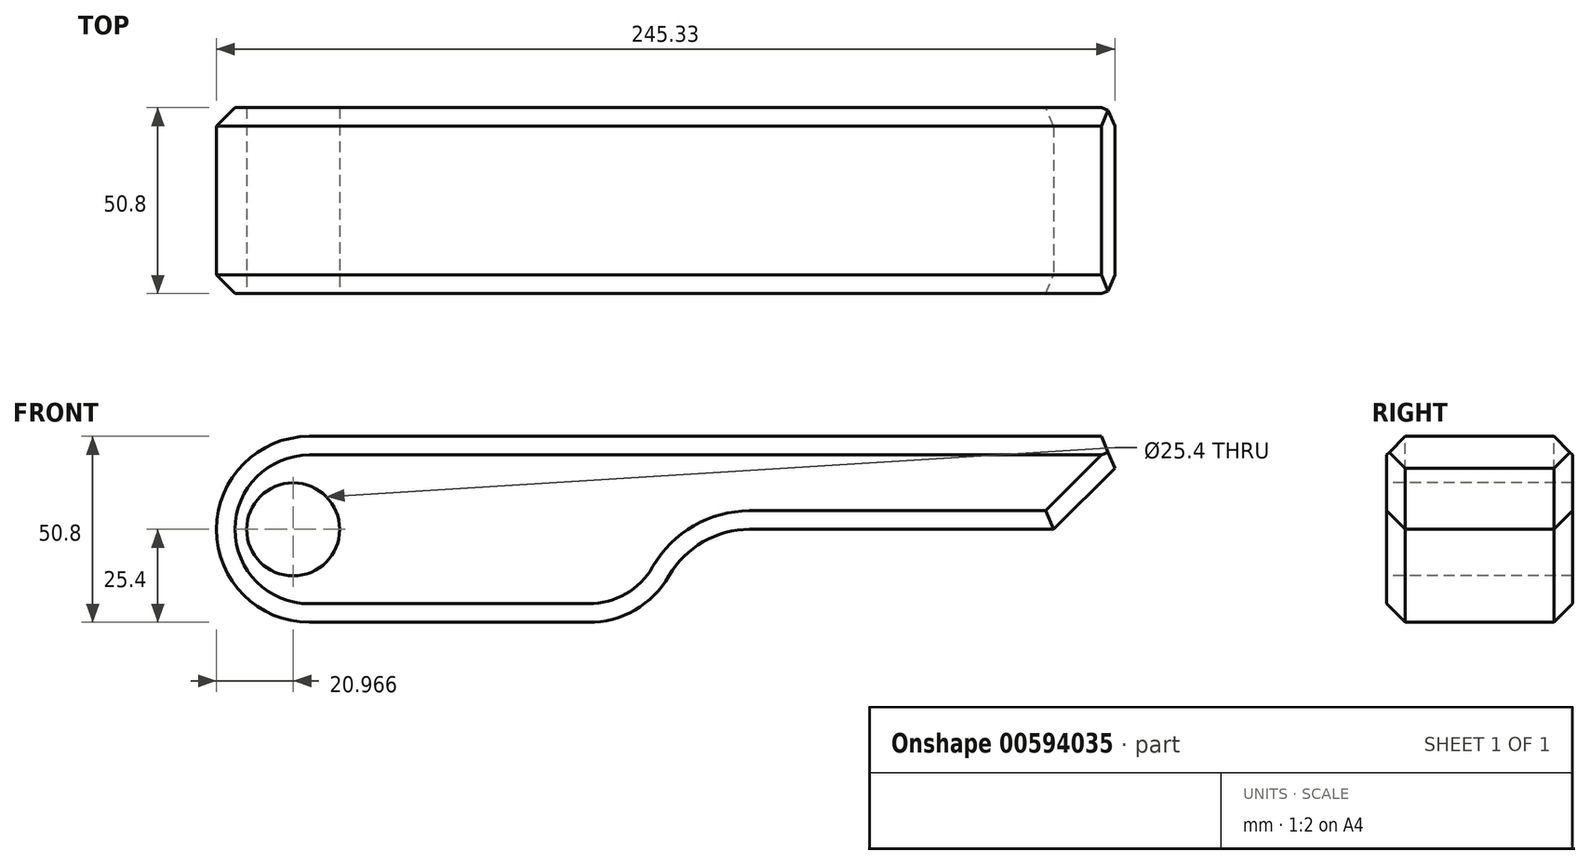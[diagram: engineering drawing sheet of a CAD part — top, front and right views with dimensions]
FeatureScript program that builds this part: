
annotation { "Feature Type Name" : "Feature", "Feature Type Description" : "" }
export const myFeature = defineFeature(function(context is Context, id is Id, definition is map)
    precondition{}
    {
        {
            var Q0;
            Q0=qCreatedBy(makeId("Top.planeOp"),FACE);
            var sketch = newSketch(context, id + "F0", { "sketchPlane" : qUnion([Q0])});
            skLineSegment(sketch, "E0.bottom", {"start": v(-73.3, 15.9) * mm, "end": v(180.7, 15.9) * mm});
            skLineSegment(sketch, "E0.top", {"start": v(-73.3, -34.9) * mm, "end": v(180.7, -34.9) * mm});
            skLineSegment(sketch, "E0.left", {"start": v(-73.3, 15.9) * mm, "end": v(-73.3, -34.9) * mm});
            skLineSegment(sketch, "E0.right", {"start": v(180.7, 15.9) * mm, "end": v(180.7, -34.9) * mm});
            skSolve(sketch);
        }
        {
            var Q0;
            Q0=makeQuery(id+"F0.imprint","IMPRINT",FACE,{"disambiguationData":[TD([[makeQuery(id+"F0.imprint","IMPRINT",EDGE,{"derivedFrom":sQuery(id+"F0.wireOp",EDGE,"E0.bottom")}),-1.0]])]});
            extrude(context, id + "F1", {"entities" : qUnion([Q0]), "depth" : 25.4 * mm, "offsetDistance" : 25.4 * mm});
        }
        {
            var Q0;
            Q0=makeQuery(id+"F1.opExtrude","CAP_FACE",FACE,{"disambiguationData":[OSD([sQuery(id+"F0.wireOp",EDGE,"E0.bottom"),sQuery(id+"F0.wireOp",EDGE,"E0.top"),sQuery(id+"F0.wireOp",EDGE,"E0.left"),sQuery(id+"F0.wireOp",EDGE,"E0.right")])],"isStart":true});
            var sketch = newSketch(context, id + "F2", { "sketchPlane" : qUnion([Q0])});
            skLineSegment(sketch, "E1.bottom", {"start": v(-73.3, 34.9) * mm, "end": v(53.7, 34.9) * mm});
            skLineSegment(sketch, "E1.top", {"start": v(-73.3, -15.9) * mm, "end": v(53.7, -15.9) * mm});
            skLineSegment(sketch, "E1.left", {"start": v(-73.3, 34.9) * mm, "end": v(-73.3, -15.9) * mm});
            skLineSegment(sketch, "E1.right", {"start": v(53.7, 34.9) * mm, "end": v(53.7, -15.9) * mm});
            skSolve(sketch);
        }
        {
            var Q0;
            Q0=makeQuery(id+"F2.imprint","IMPRINT",FACE,{"disambiguationData":[TD([[makeQuery(id+"F2.imprint","IMPRINT",EDGE,{"derivedFrom":sQuery(id+"F2.wireOp",EDGE,"E1.bottom")}),-1.0]])]});
            extrude(context, id + "F3", {"entities" : qUnion([Q0]), "operationType" : NewBodyOperationType.ADD, "depth" : 25.4 * mm, "offsetDistance" : 25.4 * mm});
        }
        {
            var Q0;
            Q0=makeQuery(id+"F3.boolean.opBoolean","MERGE",FACE,{"derivedFrom":[makeQuery(id+"F1.opExtrude","SWEPT_FACE",FACE,{"disambiguationData":[OSD([sQuery(id+"F0.wireOp",EDGE,"E0.top")])]}),makeQuery(id+"F3.opExtrude","SWEPT_FACE",FACE,{"disambiguationData":[OSD([sQuery(id+"F2.wireOp",EDGE,"E1.bottom")])]})]});
            var sketch = newSketch(context, id + "F4", { "sketchPlane" : qUnion([Q0])});
            skLineSegment(sketch, "E2", {"start": v(-73.3, 0) * mm, "end": v(53.7, 0) * mm});
            skSolve(sketch);
        }
        {
            var Q0;
            Q0=makeQuery(id+"F3.opExtrude","CAP_EDGE",EDGE,{"disambiguationData":[OSD([sQuery(id+"F2.wireOp",EDGE,"E1.left")])],"isStart":false});
            var Q1;
            Q1=makeQuery(id+"F1.opExtrude","CAP_EDGE",EDGE,{"disambiguationData":[OSD([sQuery(id+"F0.wireOp",EDGE,"E0.left")])],"isStart":false});
            fillet(context, id + "F5", {"entities" : qUnion([Q0, Q1]), "radius" : 25.4 * mm, "tangentPropagation" : true, "allowEdgeOverflow" : false});
        }
        {
            var Q0;
            Q0=makeQuery(id+"F3.opExtrude","CAP_EDGE",EDGE,{"disambiguationData":[OSD([sQuery(id+"F2.wireOp",EDGE,"E1.right")])],"isStart":false});
            fillet(context, id + "F6", {"entities" : qUnion([Q0]), "radius" : 25.4 * mm, "tangentPropagation" : true, "allowEdgeOverflow" : false});
        }
        {
            var Q0;
            {var subQ0=sQuery(id+"F4.wireOp",EDGE,"E2");Q0=makeQuery(id+"F4.imprint","IMPRINT",FACE,{"disambiguationData":[TD([[makeQuery(id+"F4.imprint","IMPRINT",EDGE,{"derivedFrom":subQ0}),-1.0]])]});}
            var sketch = newSketch(context, id + "F7", { "sketchPlane" : qUnion([Q0])});
            skCircle(sketch, "E3", {"center": v(-52.33, 0) * mm, "radius": 12.7 * mm});
            skSolve(sketch);
        }
        {
            var Q0;
            Q0=sQuery(id+"F7.wireOp",VERTEX,"E3.center");
            var Q1;
            Q1=makeQuery(id+"F1.opExtrude","SWEPT_BODY",BODY,{"disambiguationData":[OSD([sQuery(id+"F0.wireOp",EDGE,"E0.bottom"),sQuery(id+"F0.wireOp",EDGE,"E0.top"),sQuery(id+"F0.wireOp",EDGE,"E0.left"),sQuery(id+"F0.wireOp",EDGE,"E0.right")])]});
            hole(context, id + "F8", {"style" : HoleStyle.SIMPLE, "endStyle" : HoleEndStyle.BLIND, "holeDiameter" : 25.4 * mm, "majorDiameter" : 6.35 * mm, "holeDepth" : 50.8 * mm, "isTappedThrough" : true, "tappedDepth" : 12.7 * mm, "tapClearance" : 3, "locations" : qUnion([Q0]), "scope" : qUnion([Q1])});
        }
        {
            var Q0;
            Q0=makeQuery(id+"F6.opFillet","BLEND_EDGE",EDGE,{"blendedFrom":[makeQuery(id+"F3.opExtrude","CAP_EDGE",EDGE,{"disambiguationData":[OSD([sQuery(id+"F2.wireOp",EDGE,"E1.right")])],"isStart":false}),makeQuery(id+"F1.opExtrude","CAP_FACE",FACE,{"disambiguationData":[OSD([sQuery(id+"F0.wireOp",EDGE,"E0.bottom"),sQuery(id+"F0.wireOp",EDGE,"E0.top"),sQuery(id+"F0.wireOp",EDGE,"E0.left"),sQuery(id+"F0.wireOp",EDGE,"E0.right")])],"isStart":true})],"blendedInto":[makeQuery(id+"F1.opExtrude","CAP_FACE",FACE,{"disambiguationData":[OSD([sQuery(id+"F0.wireOp",EDGE,"E0.bottom"),sQuery(id+"F0.wireOp",EDGE,"E0.top"),sQuery(id+"F0.wireOp",EDGE,"E0.left"),sQuery(id+"F0.wireOp",EDGE,"E0.right")])],"isStart":true})]});
            fillet(context, id + "F9", {"entities" : qUnion([Q0]), "radius" : 25.4 * mm, "tangentPropagation" : true, "allowEdgeOverflow" : false});
        }
        {
            var Q0;
            Q0=makeQuery(id+"F1.opExtrude","CAP_EDGE",EDGE,{"disambiguationData":[OSD([sQuery(id+"F0.wireOp",EDGE,"E0.right")])],"isStart":true});
            chamfer(context, id + "F10", {"entities" : qUnion([Q0]), "width" : 25.4 * mm, "tangentPropagation" : true});
        }
        {
            var Q0;
            {var subQ0=sQuery(id+"F0.wireOp",EDGE,"E0.right");Q0=makeQuery(id+"F10.opChamfer","BLEND_EDGE",EDGE,{"blendedFrom":[makeQuery(id+"F1.opExtrude","CAP_EDGE",EDGE,{"disambiguationData":[OSD([subQ0])],"isStart":true}),makeQuery(id+"F1.opExtrude","CAP_FACE",FACE,{"disambiguationData":[OSD([sQuery(id+"F0.wireOp",EDGE,"E0.bottom"),sQuery(id+"F0.wireOp",EDGE,"E0.top"),sQuery(id+"F0.wireOp",EDGE,"E0.left"),subQ0])],"isStart":false})],"blendedInto":[makeQuery(id+"F1.opExtrude","CAP_FACE",FACE,{"disambiguationData":[OSD([sQuery(id+"F0.wireOp",EDGE,"E0.bottom"),sQuery(id+"F0.wireOp",EDGE,"E0.top"),sQuery(id+"F0.wireOp",EDGE,"E0.left"),subQ0])],"isStart":false})]});}
            var Q1;
            Q1=makeQuery(id+"F1.opExtrude","CAP_EDGE",EDGE,{"disambiguationData":[OSD([sQuery(id+"F0.wireOp",EDGE,"E0.bottom")])],"isStart":false});
            var Q2;
            Q2=makeQuery(id+"F1.opExtrude","CAP_EDGE",EDGE,{"disambiguationData":[OSD([sQuery(id+"F0.wireOp",EDGE,"E0.top")])],"isStart":false});
            var Q3;
            {var subQ0=sQuery(id+"F0.wireOp",EDGE,"E0.left");Q3=makeQuery(id+"F5.opFillet","BLEND_EDGE",EDGE,{"blendedFrom":[makeQuery(id+"F1.opExtrude","CAP_EDGE",EDGE,{"disambiguationData":[OSD([subQ0])],"isStart":false}),makeQuery(id+"F1.opExtrude","CAP_FACE",FACE,{"disambiguationData":[OSD([sQuery(id+"F0.wireOp",EDGE,"E0.bottom"),sQuery(id+"F0.wireOp",EDGE,"E0.top"),subQ0,sQuery(id+"F0.wireOp",EDGE,"E0.right")])],"isStart":false})],"blendedInto":[makeQuery(id+"F1.opExtrude","CAP_FACE",FACE,{"disambiguationData":[OSD([sQuery(id+"F0.wireOp",EDGE,"E0.bottom"),sQuery(id+"F0.wireOp",EDGE,"E0.top"),subQ0,sQuery(id+"F0.wireOp",EDGE,"E0.right")])],"isStart":false})]});}
            chamfer(context, id + "F11", {"entities" : qUnion([Q0, Q1, Q2, Q3]), "width" : 5.08 * mm, "tangentPropagation" : true});
        }
        {
            var Q0;
            Q0=makeQuery(id+"F10.opChamfer","BLEND_EDGE",EDGE,{"blendedFrom":[makeQuery(id+"F1.opExtrude","CAP_EDGE",EDGE,{"disambiguationData":[OSD([sQuery(id+"F0.wireOp",EDGE,"E0.right")])],"isStart":true}),makeQuery(id+"F3.boolean.opBoolean","MERGE",FACE,{"derivedFrom":[makeQuery(id+"F1.opExtrude","SWEPT_FACE",FACE,{"disambiguationData":[OSD([sQuery(id+"F0.wireOp",EDGE,"E0.top")])]}),makeQuery(id+"F3.opExtrude","SWEPT_FACE",FACE,{"disambiguationData":[OSD([sQuery(id+"F2.wireOp",EDGE,"E1.bottom")])]})]})],"blendedInto":[makeQuery(id+"F3.boolean.opBoolean","MERGE",FACE,{"derivedFrom":[makeQuery(id+"F1.opExtrude","SWEPT_FACE",FACE,{"disambiguationData":[OSD([sQuery(id+"F0.wireOp",EDGE,"E0.top")])]}),makeQuery(id+"F3.opExtrude","SWEPT_FACE",FACE,{"disambiguationData":[OSD([sQuery(id+"F2.wireOp",EDGE,"E1.bottom")])]})]})]});
            var Q1;
            Q1=makeQuery(id+"F10.opChamfer","BLEND_EDGE",EDGE,{"blendedFrom":[makeQuery(id+"F1.opExtrude","CAP_EDGE",EDGE,{"disambiguationData":[OSD([sQuery(id+"F0.wireOp",EDGE,"E0.right")])],"isStart":true}),makeQuery(id+"F3.boolean.opBoolean","MERGE",FACE,{"derivedFrom":[makeQuery(id+"F1.opExtrude","SWEPT_FACE",FACE,{"disambiguationData":[OSD([sQuery(id+"F0.wireOp",EDGE,"E0.bottom")])]}),makeQuery(id+"F3.opExtrude","SWEPT_FACE",FACE,{"disambiguationData":[OSD([sQuery(id+"F2.wireOp",EDGE,"E1.top")])]})]})],"blendedInto":[makeQuery(id+"F3.boolean.opBoolean","MERGE",FACE,{"derivedFrom":[makeQuery(id+"F1.opExtrude","SWEPT_FACE",FACE,{"disambiguationData":[OSD([sQuery(id+"F0.wireOp",EDGE,"E0.bottom")])]}),makeQuery(id+"F3.opExtrude","SWEPT_FACE",FACE,{"disambiguationData":[OSD([sQuery(id+"F2.wireOp",EDGE,"E1.top")])]})]})]});
            chamfer(context, id + "F12", {"entities" : qUnion([Q0, Q1]), "width" : 5.08 * mm, "tangentPropagation" : true});
        }
    });
